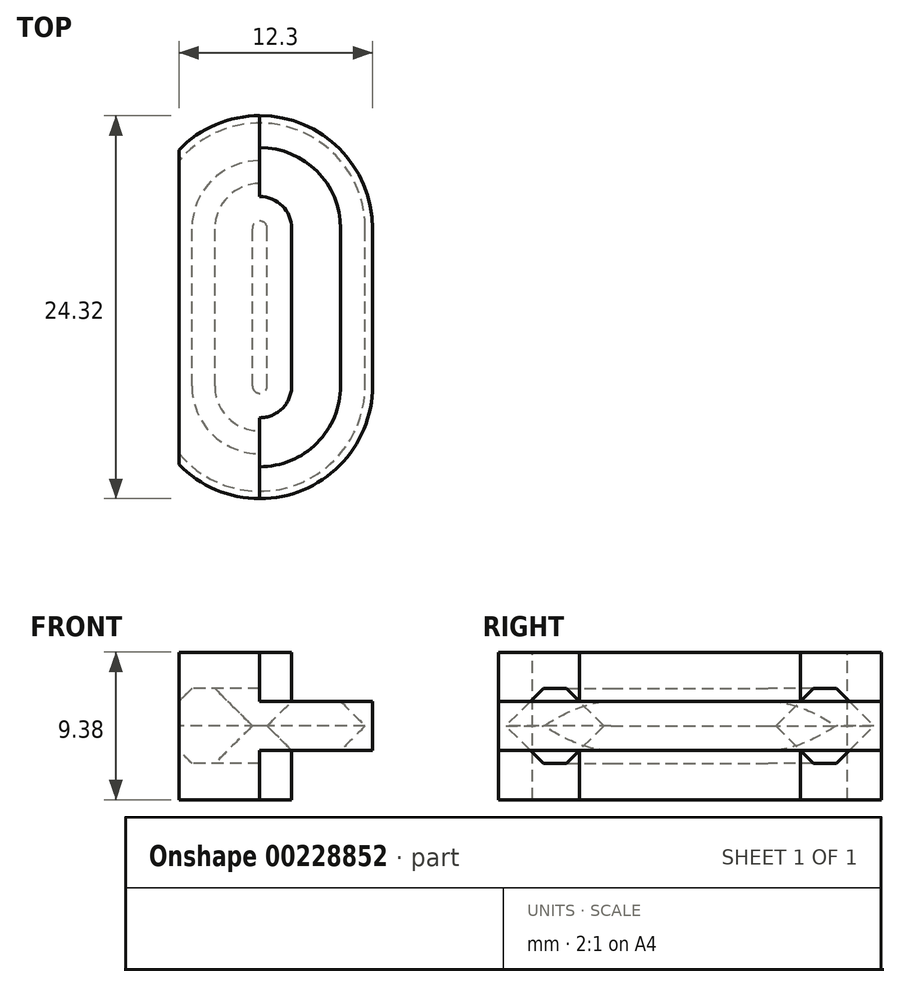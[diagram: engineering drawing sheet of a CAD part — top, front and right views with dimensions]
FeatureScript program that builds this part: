
annotation { "Feature Type Name" : "Feature", "Feature Type Description" : "" }
export const myFeature = defineFeature(function(context is Context, id is Id, definition is map)
    precondition{}
    {
        {
            var Q0;
            Q0=qCreatedBy(makeId("Top.planeOp"),FACE);
            var sketch = newSketch(context, id + "F0", { "sketchPlane" : qUnion([Q0])});
            skLineSegment(sketch, "E0.left", {"start": v(3.58, 5) * mm, "end": v(3.58, -5) * mm});
            skLineSegment(sketch, "E0.right", {"start": v(-3.58, 5) * mm, "end": v(-3.58, -5) * mm});
            skPoint(sketch, "E0.middle", {"position": v(0, 0) * mm});
            skArc(sketch, "E1", {"start": v(3.58, 5) * mm, "mid": v(0, 8.58) * mm, "end": v(-3.58, 5) * mm});
            skArc(sketch, "E2", {"start": v(-3.58, -5) * mm, "mid": v(0, -8.58) * mm, "end": v(3.58, -5) * mm});
            skLineSegment(sketch, "E3.0", {"start": v(-5.78, 5) * mm, "end": v(-5.78, -5) * mm, "construction": true});
            skArc(sketch, "E3.1", {"start": v(5.78, 5) * mm, "mid": v(0, 10.78) * mm, "end": v(-5.78, 5) * mm, "construction": true});
            skLineSegment(sketch, "E3.2", {"start": v(5.78, 5) * mm, "end": v(5.78, -5) * mm, "construction": true});
            skArc(sketch, "E3.3", {"start": v(-5.78, -5) * mm, "mid": v(0, -10.78) * mm, "end": v(5.78, -5) * mm, "construction": true});
            skArc(sketch, "E4.0", {"start": v(1.38, 5) * mm, "mid": v(0, 6.38) * mm, "end": v(-1.38, 5) * mm, "construction": true});
            skLineSegment(sketch, "E4.1", {"start": v(1.38, 5) * mm, "end": v(1.38, -5) * mm, "construction": true});
            skArc(sketch, "E4.2", {"start": v(-1.38, -5) * mm, "mid": v(0, -6.38) * mm, "end": v(1.38, -5) * mm, "construction": true});
            skLineSegment(sketch, "E4.3", {"start": v(-1.38, 5) * mm, "end": v(-1.38, -5) * mm, "construction": true});
            skLineSegment(sketch, "E5", {"start": v(-5.78, 5) * mm, "end": v(5.78, 5) * mm, "construction": true});
            skLineSegment(sketch, "E6", {"start": v(-5.78, -5) * mm, "end": v(5.78, -5) * mm, "construction": true});
            skSolve(sketch);
        }
        {
            var Q0;
            Q0=qCreatedBy(makeId("Front.planeOp"),FACE);
            var sketch = newSketch(context, id + "F1", { "sketchPlane" : qUnion([Q0])});
            skLineSegment(sketch, "E7.0", {"start": v(3.58, 0) * mm, "end": v(3.58, 0) * mm});
            skLineSegment(sketch, "E7.1", {"start": v(-3.58, 0) * mm, "end": v(-3.58, 0) * mm, "construction": true});
            skPoint(sketch, "E7.2", {"position": v(0, 0) * mm});
            skLineSegment(sketch, "E7.3", {"start": v(3.58, 0) * mm, "end": v(-3.58, 0) * mm});
            skLineSegment(sketch, "E7.4", {"start": v(-3.58, 0) * mm, "end": v(3.58, 0) * mm});
            skLineSegment(sketch, "E7.5", {"start": v(-5.78, 0) * mm, "end": v(-5.78, 0) * mm, "construction": true});
            skLineSegment(sketch, "E7.6", {"start": v(5.78, 0) * mm, "end": v(-5.78, 0) * mm});
            skLineSegment(sketch, "E7.7", {"start": v(5.78, 0) * mm, "end": v(5.78, 0) * mm});
            skLineSegment(sketch, "E7.8", {"start": v(-5.78, 0) * mm, "end": v(5.78, 0) * mm});
            skLineSegment(sketch, "E7.9", {"start": v(1.38, 0) * mm, "end": v(-1.38, 0) * mm});
            skLineSegment(sketch, "E7.10", {"start": v(1.38, 0) * mm, "end": v(1.38, 0) * mm});
            skLineSegment(sketch, "E7.11", {"start": v(-1.38, 0) * mm, "end": v(1.38, 0) * mm});
            skLineSegment(sketch, "E7.12", {"start": v(-1.38, 0) * mm, "end": v(-1.38, 0) * mm, "construction": true});
            skLineSegment(sketch, "E7.13", {"start": v(-5.78, 0) * mm, "end": v(5.78, 0) * mm});
            skLineSegment(sketch, "E7.14", {"start": v(-5.78, 0) * mm, "end": v(5.78, 0) * mm});
            skCircle(sketch, "E8", {"center": v(-3.58, 0) * mm, "radius": 2.2 * mm, "construction": true});
            skLineSegment(sketch, "E9.0", {"start": v(-3.58, 3.11) * mm, "end": v(-0.47, 0) * mm, "construction": true});
            skLineSegment(sketch, "E9.1", {"start": v(-0.47, 0) * mm, "end": v(-3.58, -3.11) * mm, "construction": true});
            skLineSegment(sketch, "E9.2", {"start": v(-3.58, -3.11) * mm, "end": v(-6.7, 0) * mm, "construction": true});
            skLineSegment(sketch, "E9.3", {"start": v(-6.7, 0) * mm, "end": v(-3.58, 3.11) * mm, "construction": true});
            skPoint(sketch, "E9.0.midPoint", {"position": v(-2.03, 1.56) * mm});
            skLineSegment(sketch, "E10", {"start": v(-2.03, 1.56) * mm, "end": v(-0.47, 0) * mm});
            skLineSegment(sketch, "E11", {"start": v(-2.03, -1.56) * mm, "end": v(-0.47, 0) * mm});
            skLineSegment(sketch, "E12", {"start": v(-2.03, -1.56) * mm, "end": v(0, -1.56) * mm});
            skLineSegment(sketch, "E13", {"start": v(0, -1.56) * mm, "end": v(0, 1.56) * mm});
            skLineSegment(sketch, "E14", {"start": v(0, 1.56) * mm, "end": v(-2.03, 1.56) * mm});
            skLineSegment(sketch, "E15", {"start": v(-3.58, 3.11) * mm, "end": v(-3.58, -3.11) * mm, "construction": true});
            skLineSegment(sketch, "E16.MirrorCS", {"start": v(-5.14, -1.56) * mm, "end": v(-7.16, -1.56) * mm});
            skLineSegment(sketch, "E17.MirrorCS", {"start": v(-7.16, 1.56) * mm, "end": v(-5.14, 1.56) * mm});
            skLineSegment(sketch, "E18.MirrorCS", {"start": v(-7.16, -1.56) * mm, "end": v(-7.16, 1.56) * mm});
            skLineSegment(sketch, "E19", {"start": v(-5.14, 1.56) * mm, "end": v(-6.7, 0) * mm});
            skLineSegment(sketch, "E20", {"start": v(-5.14, -1.56) * mm, "end": v(-6.7, 0) * mm});
            skSolve(sketch);
        }
        {
            var Q0;
            Q0=sQuery(id+"F0.wireOp",VERTEX,"E3.1.end");
            var Q1;
            Q1=makeQuery(id+"F1.imprint","IMPRINT",FACE,{"disambiguationData":[TD([[makeQuery(id+"F1.imprint","IMPRINT",EDGE,{"derivedFrom":sQuery(id+"F1.wireOp",EDGE,"E16.MirrorCS")}),-1.0]])]});
            cPlane(context, id + "F2", {"entities" : qUnion([Q0, Q1]), "cplaneType" : CPlaneType.PLANE_POINT, "offset" : 25 * mm, "width" : 150 * mm, "height" : 150 * mm});
        }
        {
            var Q0;
            Q0=qCreatedBy(id+"F2.planeOp",FACE);
            var sketch = newSketch(context, id + "F3", { "sketchPlane" : qUnion([Q0])});
            skLineSegment(sketch, "E21.0", {"start": v(3.58, 0) * mm, "end": v(3.58, 0) * mm});
            skLineSegment(sketch, "E21.1", {"start": v(-3.58, 0) * mm, "end": v(-3.58, 0) * mm});
            skPoint(sketch, "E21.2", {"position": v(0, 0) * mm});
            skLineSegment(sketch, "E21.3", {"start": v(3.58, 0) * mm, "end": v(0, 0) * mm});
            skLineSegment(sketch, "E21.4", {"start": v(-3.58, 0) * mm, "end": v(-1.38, 0) * mm});
            skLineSegment(sketch, "E21.5", {"start": v(-5.78, 0) * mm, "end": v(-5.78, 0) * mm});
            skLineSegment(sketch, "E21.6", {"start": v(5.78, 0) * mm, "end": v(0, 0) * mm});
            skLineSegment(sketch, "E21.7", {"start": v(5.78, 0) * mm, "end": v(5.78, 0) * mm});
            skLineSegment(sketch, "E21.8", {"start": v(-5.78, 0) * mm, "end": v(-1.38, 0) * mm});
            skLineSegment(sketch, "E21.9", {"start": v(1.38, 0) * mm, "end": v(0, 0) * mm});
            skLineSegment(sketch, "E21.10", {"start": v(1.38, 0) * mm, "end": v(1.38, 0) * mm});
            skLineSegment(sketch, "E21.12", {"start": v(-1.38, 0) * mm, "end": v(-1.38, 0) * mm});
            skLineSegment(sketch, "E21.13", {"start": v(-5.78, 0) * mm, "end": v(-1.38, 0) * mm});
            skLineSegment(sketch, "E21.14", {"start": v(-5.78, 0) * mm, "end": v(-1.38, 0) * mm});
            skCircle(sketch, "E21.15", {"center": v(-3.58, 0) * mm, "radius": 2.2 * mm});
            skCircle(sketch, "E21.16", {"center": v(-3.58, 0) * mm, "radius": 2.2 * mm});
            skLineSegment(sketch, "E21.17", {"start": v(-3.58, 3.11) * mm, "end": v(-0.47, 0) * mm});
            skLineSegment(sketch, "E21.18", {"start": v(-0.47, 0) * mm, "end": v(-3.58, -3.11) * mm});
            skLineSegment(sketch, "E21.19", {"start": v(-3.58, -3.11) * mm, "end": v(-6.7, 0) * mm});
            skLineSegment(sketch, "E21.20", {"start": v(-6.7, 0) * mm, "end": v(-3.58, 3.11) * mm});
            skPoint(sketch, "E21.21", {"position": v(-2.03, 1.56) * mm});
            skLineSegment(sketch, "E21.22", {"start": v(-2.03, 1.56) * mm, "end": v(-0.47, 0) * mm});
            skLineSegment(sketch, "E21.23", {"start": v(-2.03, -1.56) * mm, "end": v(-0.47, 0) * mm});
            skLineSegment(sketch, "E21.24", {"start": v(-2.03, -1.56) * mm, "end": v(0, -1.56) * mm});
            skLineSegment(sketch, "E21.25", {"start": v(0, -1.56) * mm, "end": v(0, 1.56) * mm});
            skLineSegment(sketch, "E21.27", {"start": v(-3.58, 3.11) * mm, "end": v(-3.58, -3.11) * mm});
            skLineSegment(sketch, "E21.28", {"start": v(-5.14, -1.56) * mm, "end": v(-7.16, -1.56) * mm});
            skLineSegment(sketch, "E21.30", {"start": v(-7.16, -1.56) * mm, "end": v(-7.16, 1.56) * mm});
            skLineSegment(sketch, "E21.31", {"start": v(-5.14, 1.56) * mm, "end": v(-6.7, 0) * mm});
            skLineSegment(sketch, "E21.32", {"start": v(-5.14, -1.56) * mm, "end": v(-6.7, 0) * mm});
            skLineSegment(sketch, "E22.trimOffspring", {"start": v(0, 0) * mm, "end": v(5.78, 0) * mm});
            skLineSegment(sketch, "E23.trimOffspring", {"start": v(0, 0) * mm, "end": v(1.38, 0) * mm});
            skPoint(sketch, "E21.11.start.orphan", {"position": v(-1.38, 0) * mm});
            skLineSegment(sketch, "E24.trimOffspring", {"start": v(-1.38, 0) * mm, "end": v(-5.78, 0) * mm});
            skLineSegment(sketch, "E25.trimOffspring", {"start": v(0, 0) * mm, "end": v(3.58, 0) * mm});
            skLineSegment(sketch, "E26.trimOffspring", {"start": v(-1.38, 0) * mm, "end": v(-3.58, 0) * mm});
            skLineSegment(sketch, "E27", {"start": v(0, 7.87) * mm, "end": v(0, -7.9) * mm});
            skLineSegment(sketch, "E28", {"start": v(-7.16, 1.56) * mm, "end": v(-7.16, 4.69) * mm});
            skLineSegment(sketch, "E29", {"start": v(-7.16, 4.69) * mm, "end": v(0, 4.69) * mm});
            skLineSegment(sketch, "E30", {"start": v(0, 4.69) * mm, "end": v(0, 1.56) * mm});
            skPoint(sketch, "E21.29.end.orphan", {"position": v(-5.14, 1.56) * mm});
            skPoint(sketch, "E21.26.end.orphan", {"position": v(-2.03, 1.56) * mm});
            skPoint(sketch, "E21.26.start.orphan", {"position": v(0, 1.56) * mm});
            skLineSegment(sketch, "E31.MirrorCS", {"start": v(-7.16, -4.69) * mm, "end": v(0, -4.69) * mm});
            skLineSegment(sketch, "E32.MirrorCS", {"start": v(-7.16, -1.56) * mm, "end": v(-7.16, -4.69) * mm});
            skLineSegment(sketch, "E33", {"start": v(-4.3, 2.39) * mm, "end": v(-2.86, 2.39) * mm});
            skLineSegment(sketch, "E34.MirrorCS", {"start": v(-4.3, -2.39) * mm, "end": v(-2.86, -2.39) * mm});
            skSolve(sketch);
        }
        {
            var Q0;
            Q0=makeQuery(id+"F3.imprint","IMPRINT",FACE,{"disambiguationData":[TD([[makeQuery(id+"F3.imprint","IMPRINT",EDGE,{"derivedFrom":sQuery(id+"F3.wireOp",EDGE,"E21.28")}),-1.0]])]});
            var Q1;
            Q1=makeQuery(id+"F3.imprint","IMPRINT",FACE,{"disambiguationData":[TD([[makeQuery(id+"F3.imprint","IMPRINT",EDGE,{"derivedFrom":sQuery(id+"F3.wireOp",EDGE,"E21.22")}),1.0]])]});
            var Q2;
            {var subQ9=sQuery(id+"F3.wireOp",EDGE,"E21.24");Q2=makeQuery(id+"F3.imprint","IMPRINT",FACE,{"disambiguationData":[TD([[makeQuery(id+"F3.imprint","IMPRINT",EDGE,{"derivedFrom":subQ9}),-1.0]])]});}
            var Q3;
            {var subQ1=sQuery(id+"F3.wireOp",EDGE,"E21.18");var subQ3=sQuery(id+"F3.wireOp",EDGE,"E34.MirrorCS");var subQ4=makeQuery(id+"F3.imprint","INTERSECT",VERTEX,{"derivedFrom":[subQ1,subQ3]});Q3=makeQuery(id+"F3.imprint","IMPRINT",FACE,{"disambiguationData":[TD([[makeQuery(id+"F3.imprint","IMPRINT",EDGE,{"disambiguationData":[TD([[subQ4,1.0]])],"derivedFrom":subQ3}),-1.0]])]});}
            var Q4;
            {var subQ1=sQuery(id+"F3.wireOp",EDGE,"E21.19");var subQ3=sQuery(id+"F3.wireOp",EDGE,"E34.MirrorCS");var subQ4=makeQuery(id+"F3.imprint","INTERSECT",VERTEX,{"derivedFrom":[subQ1,subQ3]});Q4=makeQuery(id+"F3.imprint","IMPRINT",FACE,{"disambiguationData":[TD([[makeQuery(id+"F3.imprint","IMPRINT",EDGE,{"disambiguationData":[TD([[subQ4,-1.0]])],"derivedFrom":subQ3}),-1.0]])]});}
            var Q5;
            Q5=sQuery(id+"F3.wireOp",EDGE,"E27");
            var Q6;
            Q6=sQuery(id+"F3.wireOp",EDGE,"E27");
            revolve(context, id + "F4", {"entities" : qUnion([Q0, Q1, Q2, Q3, Q4]), "surfaceEntities" : qUnion([Q5]), "axis" : qUnion([Q6]), "revolveType" : RevolveType.ONE_DIRECTION, "angle" : 90 * degree});
        }
        {
            var Q0;
            Q0=makeQuery(id+"F4.opRevolve","CAP_FACE",FACE,{"disambiguationData":[OSD([sQuery(id+"F3.wireOp",EDGE,"E21.17"),sQuery(id+"F3.wireOp",EDGE,"E21.20"),sQuery(id+"F3.wireOp",EDGE,"E21.22"),sQuery(id+"F3.wireOp",EDGE,"E21.23"),sQuery(id+"F3.wireOp",EDGE,"E21.24"),sQuery(id+"F3.wireOp",EDGE,"E21.28"),sQuery(id+"F3.wireOp",EDGE,"E21.30"),sQuery(id+"F3.wireOp",EDGE,"E21.31"),sQuery(id+"F3.wireOp",EDGE,"E21.32"),sQuery(id+"F3.wireOp",EDGE,"E27"),sQuery(id+"F3.wireOp",EDGE,"E28"),sQuery(id+"F3.wireOp",EDGE,"E29"),sQuery(id+"F3.wireOp",EDGE,"E30")])],"isStart":false});
            var sketch = newSketch(context, id + "F5", { "sketchPlane" : qUnion([Q0])});
            skLineSegment(sketch, "E35.0", {"start": v(8.58, 3.11) * mm, "end": v(5.47, 0) * mm});
            skLineSegment(sketch, "E36.0", {"start": v(8.58, 3.11) * mm, "end": v(11.7, 0) * mm});
            skLineSegment(sketch, "E36.1", {"start": v(11.7, 0) * mm, "end": v(11.7, 0) * mm});
            skLineSegment(sketch, "E36.2", {"start": v(5.47, 0) * mm, "end": v(5.47, 0) * mm});
            skLineSegment(sketch, "E36.4", {"start": v(5, 7.87) * mm, "end": v(5, -7.9) * mm});
            skLineSegment(sketch, "E36.5", {"start": v(12.16, 4.69) * mm, "end": v(5, 4.69) * mm});
            skLineSegment(sketch, "E36.6", {"start": v(12.16, -4.69) * mm, "end": v(12.16, 4.69) * mm});
            skLineSegment(sketch, "E37", {"start": v(7.03, 1.56) * mm, "end": v(5, 1.56) * mm});
            skLineSegment(sketch, "E38", {"start": v(10.14, 1.56) * mm, "end": v(12.16, 1.56) * mm});
            skLineSegment(sketch, "E39.MirrorCS", {"start": v(7.03, -1.56) * mm, "end": v(5, -1.56) * mm});
            skLineSegment(sketch, "E40.MirrorCS", {"start": v(10.14, -1.56) * mm, "end": v(12.16, -1.56) * mm});
            skLineSegment(sketch, "E41.0", {"start": v(7.86, -2.39) * mm, "end": v(5.47, 0) * mm});
            skLineSegment(sketch, "E41.1", {"start": v(9.3, -2.39) * mm, "end": v(11.7, 0) * mm});
            skLineSegment(sketch, "E42.0", {"start": v(9.3, -2.39) * mm, "end": v(7.86, -2.39) * mm});
            skSolve(sketch);
        }
        {
            var Q0;
            {var subQ4=sQuery(id+"F5.wireOp",EDGE,"E37");Q0=makeQuery(id+"F5.imprint","IMPRINT",FACE,{"disambiguationData":[TD([[makeQuery(id+"F5.imprint","IMPRINT",EDGE,{"derivedFrom":subQ4}),1.0]])]});}
            var Q1;
            {var subQ1=sQuery(id+"F5.wireOp",EDGE,"E38");Q1=makeQuery(id+"F5.imprint","IMPRINT",FACE,{"disambiguationData":[TD([[makeQuery(id+"F5.imprint","IMPRINT",EDGE,{"derivedFrom":subQ1}),-1.0]])]});}
            var Q2;
            Q2=sQuery(id+"F5.wireOp",EDGE,"E36.4");
            revolve(context, id + "F6", {"operationType" : NewBodyOperationType.ADD, "entities" : qUnion([Q0, Q1]), "axis" : qUnion([Q2]), "revolveType" : RevolveType.ONE_DIRECTION, "angle" : 90 * degree});
        }
        {
            var Q0;
            Q0=makeQuery(id+"F6.opRevolve","CAP_FACE",FACE,{"disambiguationData":[OSD([sQuery(id+"F5.wireOp",EDGE,"E36.0"),sQuery(id+"F5.wireOp",EDGE,"E36.1"),sQuery(id+"F5.wireOp",EDGE,"E36.6"),sQuery(id+"F5.wireOp",EDGE,"0190284d-4efd-4984-be75-bf97c9e85897.0"),sQuery(id+"F5.wireOp",EDGE,"E38")])],"isStart":false});
            var Q1;
            Q1=makeQuery(id+"F6.boolean.opBoolean","MERGE",FACE,{"derivedFrom":[makeQuery(id+"F4.opRevolve","CAP_FACE",FACE,{"disambiguationData":[OSD([sQuery(id+"F3.wireOp",EDGE,"E21.17"),sQuery(id+"F3.wireOp",EDGE,"E21.20"),sQuery(id+"F3.wireOp",EDGE,"E21.22"),sQuery(id+"F3.wireOp",EDGE,"E21.23"),sQuery(id+"F3.wireOp",EDGE,"E21.24"),sQuery(id+"F3.wireOp",EDGE,"E21.28"),sQuery(id+"F3.wireOp",EDGE,"E21.30"),sQuery(id+"F3.wireOp",EDGE,"E21.31"),sQuery(id+"F3.wireOp",EDGE,"E21.32"),sQuery(id+"F3.wireOp",EDGE,"E27"),sQuery(id+"F3.wireOp",EDGE,"E28"),sQuery(id+"F3.wireOp",EDGE,"E29"),sQuery(id+"F3.wireOp",EDGE,"E30")])],"isStart":true}),makeQuery(id+"F6.opRevolve","CAP_FACE",FACE,{"disambiguationData":[OSD([sQuery(id+"F5.wireOp",EDGE,"E35.0"),sQuery(id+"F5.wireOp",EDGE,"E36.2"),sQuery(id+"F5.wireOp",EDGE,"E36.3"),sQuery(id+"F5.wireOp",EDGE,"E36.4"),sQuery(id+"F5.wireOp",EDGE,"E37")])],"isStart":false})]});
            extrude(context, id + "F7", {"entities" : qUnion([Q0, Q1]), "operationType" : NewBodyOperationType.ADD, "depth" : 10 * mm});
        }
        {
            var Q0;
            Q0=makeQuery(id+"F4.opRevolve","SWEPT_BODY",BODY,{"disambiguationData":[OSD([sQuery(id+"F3.wireOp",EDGE,"E21.17"),sQuery(id+"F3.wireOp",EDGE,"E21.20"),sQuery(id+"F3.wireOp",EDGE,"E21.22"),sQuery(id+"F3.wireOp",EDGE,"E21.23"),sQuery(id+"F3.wireOp",EDGE,"E21.24"),sQuery(id+"F3.wireOp",EDGE,"E21.28"),sQuery(id+"F3.wireOp",EDGE,"E21.30"),sQuery(id+"F3.wireOp",EDGE,"E21.31"),sQuery(id+"F3.wireOp",EDGE,"E21.32"),sQuery(id+"F3.wireOp",EDGE,"E27"),sQuery(id+"F3.wireOp",EDGE,"E28"),sQuery(id+"F3.wireOp",EDGE,"E29"),sQuery(id+"F3.wireOp",EDGE,"E30")])]});
            var Q1;
            Q1=qCreatedBy(makeId("Front.planeOp"),FACE);
            mirror(context, id + "F8", {"operationType" : NewBodyOperationType.ADD, "entities" : qUnion([Q0]), "mirrorPlane" : qUnion([Q1])});
        }
        {
            var Q0;
            Q0=makeQuery(id+"F4.opRevolve","SWEPT_BODY",BODY,{"disambiguationData":[OSD([sQuery(id+"F3.wireOp",EDGE,"E21.17"),sQuery(id+"F3.wireOp",EDGE,"E21.20"),sQuery(id+"F3.wireOp",EDGE,"E21.22"),sQuery(id+"F3.wireOp",EDGE,"E21.23"),sQuery(id+"F3.wireOp",EDGE,"E21.24"),sQuery(id+"F3.wireOp",EDGE,"E21.28"),sQuery(id+"F3.wireOp",EDGE,"E21.30"),sQuery(id+"F3.wireOp",EDGE,"E21.31"),sQuery(id+"F3.wireOp",EDGE,"E21.32"),sQuery(id+"F3.wireOp",EDGE,"E27"),sQuery(id+"F3.wireOp",EDGE,"E28"),sQuery(id+"F3.wireOp",EDGE,"E29"),sQuery(id+"F3.wireOp",EDGE,"E30")])]});
            var Q1;
            Q1=qCreatedBy(makeId("Top.planeOp"),FACE);
            mirror(context, id + "F9", {"operationType" : NewBodyOperationType.ADD, "entities" : qUnion([Q0]), "mirrorPlane" : qUnion([Q1])});
        }
        {
            var Q0;
            {var subQ0=sQuery(id+"F5.wireOp",EDGE,"E39.MirrorCS");var subQ1=makeQuery(id+"F7.boolean.opBoolean","MERGE",FACE,{"derivedFrom":[makeQuery(id+"F6.opRevolve","SWEPT_FACE",FACE,{"disambiguationData":[OSD([subQ0])]}),makeQuery(id+"F7.opExtrude","SWEPT_FACE",FACE,{"disambiguationData":[OSD([subQ0])]})]});Q0=makeQuery(id+"F8.boolean.opBoolean","MERGE",FACE,{"derivedFrom":[subQ1,makeQuery(id+"F8.opPattern","COPY",FACE,{"derivedFrom":subQ1,"instanceName":"1"})]});}
            var Q1;
            {var subQ0=sQuery(id+"F3.wireOp",EDGE,"E31.MirrorCS");var subQ1=makeQuery(id+"F7.boolean.opBoolean","MERGE",FACE,{"derivedFrom":[makeQuery(id+"F4.opRevolve","SWEPT_FACE",FACE,{"disambiguationData":[OSD([subQ0])]}),makeQuery(id+"F7.opExtrude","SWEPT_FACE",FACE,{"disambiguationData":[OSD([subQ0])]})]});Q1=makeQuery(id+"F8.boolean.opBoolean","MERGE",FACE,{"derivedFrom":[subQ1,makeQuery(id+"F8.opPattern","COPY",FACE,{"derivedFrom":subQ1,"instanceName":"1"})]});}
            extrude(context, id + "F10", {"entities" : qUnion([Q0]), "operationType" : NewBodyOperationType.ADD, "endBound" : BoundingType.UP_TO_SURFACE, "endBoundEntityFace" : qUnion([Q1]), "depth" : 2.18 * mm});
        }
        {
            var Q0;
            {var subQ0=sQuery(id+"F5.wireOp",EDGE,"E37");var subQ1=makeQuery(id+"F7.boolean.opBoolean","MERGE",FACE,{"derivedFrom":[makeQuery(id+"F6.opRevolve","SWEPT_FACE",FACE,{"disambiguationData":[OSD([subQ0])]}),makeQuery(id+"F7.opExtrude","SWEPT_FACE",FACE,{"disambiguationData":[OSD([subQ0])]})]});Q0=makeQuery(id+"F8.boolean.opBoolean","MERGE",FACE,{"derivedFrom":[subQ1,makeQuery(id+"F8.opPattern","COPY",FACE,{"derivedFrom":subQ1,"instanceName":"1"})]});}
            var Q1;
            {var subQ0=sQuery(id+"F3.wireOp",EDGE,"E29");var subQ1=makeQuery(id+"F7.boolean.opBoolean","MERGE",FACE,{"derivedFrom":[makeQuery(id+"F4.opRevolve","SWEPT_FACE",FACE,{"disambiguationData":[OSD([subQ0])]}),makeQuery(id+"F7.opExtrude","SWEPT_FACE",FACE,{"disambiguationData":[OSD([subQ0])]})]});Q1=makeQuery(id+"F8.boolean.opBoolean","MERGE",FACE,{"derivedFrom":[subQ1,makeQuery(id+"F8.opPattern","COPY",FACE,{"derivedFrom":subQ1,"instanceName":"1"})]});}
            extrude(context, id + "F11", {"entities" : qUnion([Q0]), "operationType" : NewBodyOperationType.ADD, "endBound" : BoundingType.UP_TO_SURFACE, "endBoundEntityFace" : qUnion([Q1]), "depth" : 25 * mm});
        }
        {
            var Q0;
            Q0=qCreatedBy(makeId("Front.planeOp"),FACE);
            var sketch = newSketch(context, id + "F12", { "sketchPlane" : qUnion([Q0])});
            skFitSpline(sketch, "E43.0", {"points": [v(-4.3, -2.39) * mm, v(-5.1, -1.6) * mm, v(-5.9, -0.8) * mm, v(-6.7, 0) * mm], "construction": true});
            skFitSpline(sketch, "E43.1", {"points": [v(-4.3, 2.39) * mm, v(-5.1, 1.6) * mm, v(-5.9, 0.8) * mm, v(-6.7, 0) * mm], "construction": true});
            skFitSpline(sketch, "E43.2", {"points": [v(-2.86, 2.39) * mm, v(-2.06, 1.6) * mm, v(-1.27, 0.8) * mm, v(-0.47, 0) * mm], "construction": true});
            skLineSegment(sketch, "E43.3", {"start": v(0, 2.39) * mm, "end": v(-4.3, 2.39) * mm, "construction": true});
            skFitSpline(sketch, "E43.4", {"points": [v(-2.86, -2.39) * mm, v(-2.06, -1.6) * mm, v(-1.27, -0.8) * mm, v(-0.47, 0) * mm], "construction": true});
            skLineSegment(sketch, "E43.5", {"start": v(0, -2.39) * mm, "end": v(-4.3, -2.39) * mm, "construction": true});
            skCircle(sketch, "E44", {"center": v(-3.58, 0) * mm, "radius": 2.2 * mm, "construction": true});
            skPoint(sketch, "E44.first.point", {"position": v(-2.03, 1.56) * mm});
            skPoint(sketch, "E44.second.point", {"position": v(-2.03, -1.56) * mm});
            skLineSegment(sketch, "E45", {"start": v(-5.14, 5.23) * mm, "end": v(-5.14, -6.18) * mm});
            skPoint(sketch, "E46", {"position": v(-5.14, -1.56) * mm});
            skLineSegment(sketch, "E47", {"start": v(-5.14, 5.23) * mm, "end": v(-8.75, 5.36) * mm});
            skLineSegment(sketch, "E48", {"start": v(-8.75, 5.36) * mm, "end": v(-9.49, -3.83) * mm});
            skLineSegment(sketch, "E49", {"start": v(-9.49, -3.83) * mm, "end": v(-5.14, -6.18) * mm});
            skSolve(sketch);
        }
        {
            var Q0;
            Q0 = qSketchRegion(id + "F12", true);
            extrude(context, id + "F13", {"entities" : qUnion([Q0]), "operationType" : NewBodyOperationType.REMOVE, "oppositeDirection" : true, "depth" : 14.5 * mm, "hasSecondDirection" : true, "secondDirectionOppositeDirection" : false, "secondDirectionDepth" : 25 * mm});
        }
    });
